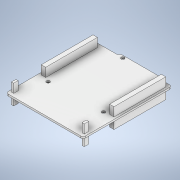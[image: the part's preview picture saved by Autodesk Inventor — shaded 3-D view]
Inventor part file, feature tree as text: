
AUTODESK INVENTOR PART (.ipt)
format: ipt  version: 2022 (Build 260153000, 153)  size: 203,776 bytes
history: native  units: mm
features: extrude x4, sketch x4, fillet x1
ambient origin geometry x8: Origin, YZ Plane, XZ Plane, XY Plane, X Axis, Y Axis, Z Axis, Center Point
bodies: Solid1 (feature_tree)
feature tree (9):
  extrude  "Extrusion1"  Depth=80.5mm
  fillet  "Fillet1"  Radius=20.51mm
  extrude  "Extrusion2"  Depth=80.5mm
  extrude  "Extrusion3"  TaperAngle=45.0deg  [1 undecoded]
  extrude  "Extrusion4"  Depth=1.65mm TaperAngle=0.0deg
  sketch  "Sketch1"  dims[d0=70.0mm d1=80.5mm d2=20.51mm]
  sketch  "Sketch2"  dims[d3=80.5mm d4=11.33mm]
  sketch  "Sketch3"  dims[d5=82.45mm d6=45.0deg]
  sketch  "Sketch4"  dims[d7=45.0deg d8=1.65mm d9=0.0mm d10=2.0mm d11=3.0mm d12=3.0mm d13=3.0mm d14=29.0mm d15=10.5mm d16=10.5mm d17=2.3mm d18=25.8mm d19=20.0mm d20=0.0mm d21=4.0mm d22=47.0mm d23=30.0mm d24=2.0mm d27=2.0mm d28=4.0mm d30=30.0mm d31=8.3mm d32=0.0mm d33=2.0mm d34=4.0mm d35=2.0mm d36=4.0mm d37=3.0mm d38=8.0mm d39=0.0mm d40=27.7mm]
note: 1 required parameter value undecoded (feature->parameter linkage not recoverable at this tier; creation-order binding heuristic only, values carry confidence <= 0.55)
